# Revit family: 10621XXX_last
name_source: partatom
category: Plumbing Fixtures
units: mm (PartAtom-declared; Revit-internal decimal feet)

## family parameters
Cut with Voids When Loaded = Yes
Host = Face
OmniClass Number = 23.31.17.00
OmniClass Title = Showers
Part Type = Normal
Room Calculation Point = No
Round Connector Dimension = Use Diameter
Shared = No

## types (3) — shared parameters
Always visible = Yes
Connector Description = Water Inlet 19.1mm
Default Elevation = 1219 mm
Description = AXOR ShowerSolutions ShowerHeaven 970/970 3jet without lighting
Diameter = 19 mm
Manufacturer = AXOR
Model = 10621XXX
Product Guid = 5b17b316-6556-4710-b6c7-a236003ff9c4
Product Page URL = https://www.axor-design.com
Product data url = https://bimobject.com
URL = https://www.axor-design.com
Version = 1

## per-type parameters (varying)
| type | Material |
| 250 Brushed Gold Optic | AXOR - Metal - 250 Brushed Gold Optic |
| 800 Stainless Steel Optic | AXOR - Metal - 800 Stainless Steel Optic |
| 990 Polished Gold Optic | AXOR - Metal - 990 Polished Gold Optic |

## geometry (parser evidence)
native form markers: Sweep x2
no freeform markers — native parametric forms only
